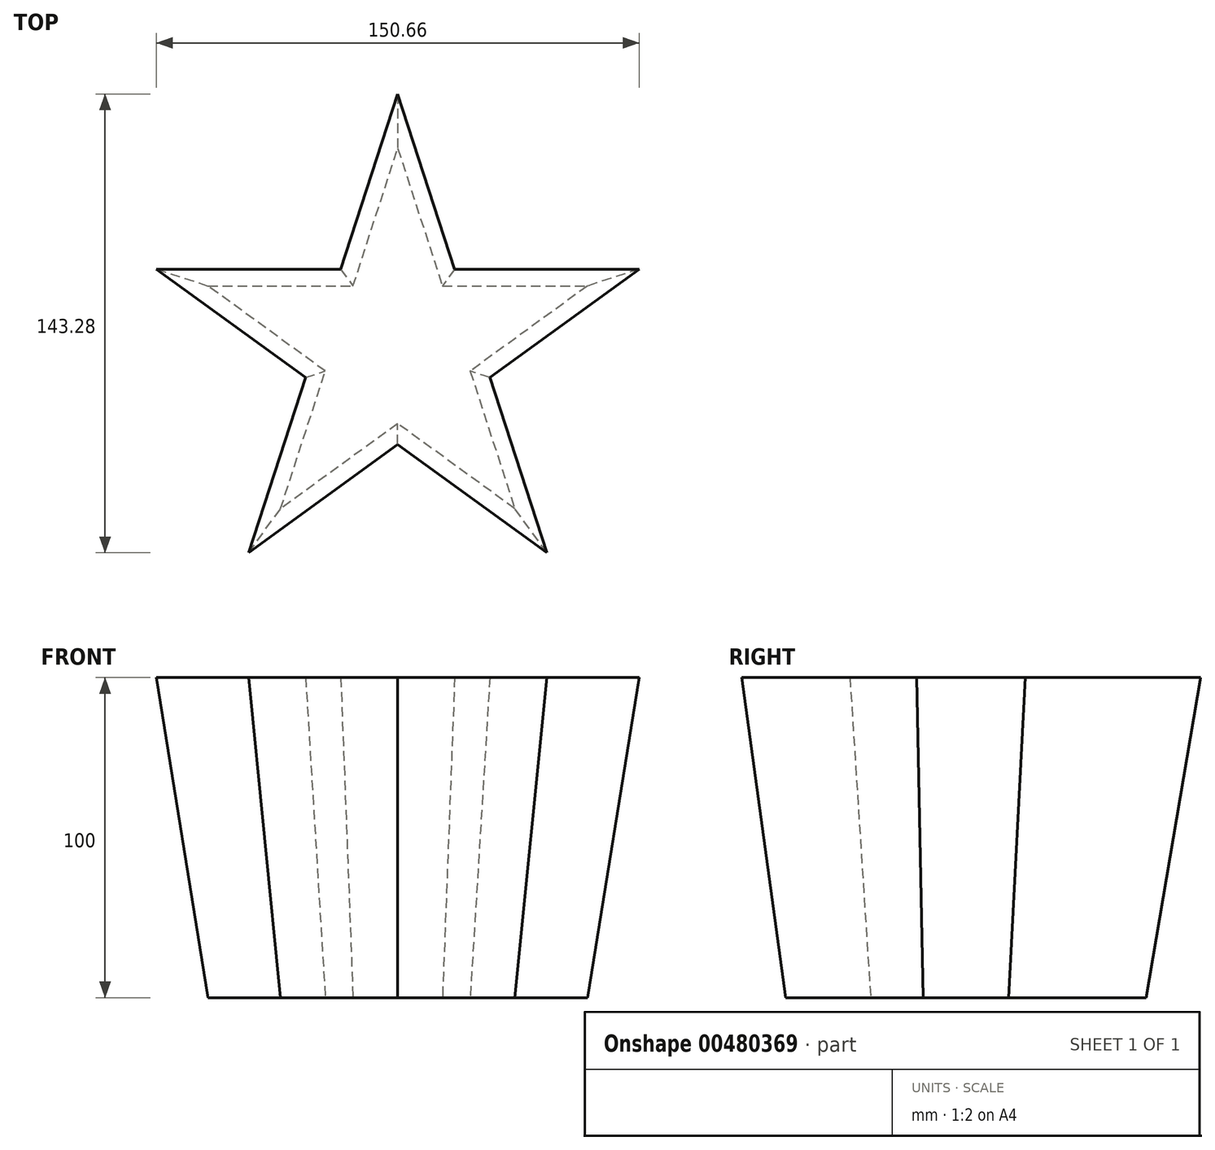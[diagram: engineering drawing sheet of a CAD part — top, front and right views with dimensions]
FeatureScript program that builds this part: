
annotation { "Feature Type Name" : "Feature", "Feature Type Description" : "" }
export const myFeature = defineFeature(function(context is Context, id is Id, definition is map)
    precondition{}
    {
        {
            var Q0;
            Q0=qCreatedBy(makeId("Top.planeOp"),FACE);
            var sketch = newSketch(context, id + "F0", { "sketchPlane" : qUnion([Q0])});
            skLineSegment(sketch, "E0.bottom", {"start": v(-74.57, -72.66) * mm, "end": v(74.57, -72.66) * mm, "construction": true});
            skLineSegment(sketch, "E0.top", {"start": v(-74.57, 66.68) * mm, "end": v(74.57, 66.68) * mm, "construction": true});
            skLineSegment(sketch, "E0.left", {"start": v(-74.57, -72.66) * mm, "end": v(-74.57, 66.68) * mm, "construction": true});
            skLineSegment(sketch, "E0.right", {"start": v(74.57, -72.66) * mm, "end": v(74.57, 66.68) * mm, "construction": true});
            skPoint(sketch, "E0.middle", {"position": v(0, -3) * mm});
            skPoint(sketch, "E1.0.midPoint", {"position": v(0, -50.36) * mm});
            skLineSegment(sketch, "E2", {"start": v(0, 62.24) * mm, "end": v(0, 0) * mm});
            skLineSegment(sketch, "E3", {"start": v(-36.59, -50.36) * mm, "end": v(59.2, 19.23) * mm});
            skLineSegment(sketch, "E4", {"start": v(59.2, 19.23) * mm, "end": v(-59.2, 19.23) * mm});
            skLineSegment(sketch, "E5", {"start": v(-59.2, 19.23) * mm, "end": v(36.59, -50.36) * mm});
            skLineSegment(sketch, "E6", {"start": v(36.59, -50.36) * mm, "end": v(0, 62.24) * mm});
            skLineSegment(sketch, "E7", {"start": v(0, 62.24) * mm, "end": v(-36.59, -50.36) * mm});
            skSolve(sketch);
        }
        {
            var Q0;
            Q0 = qSketchRegion(id + "F0", true);
            extrude(context, id + "F1", {"entities" : qUnion([Q0]), "depth" : 100 * mm, "hasDraft" : true, "draftAngle" : 3 * degree});
        }
    });
